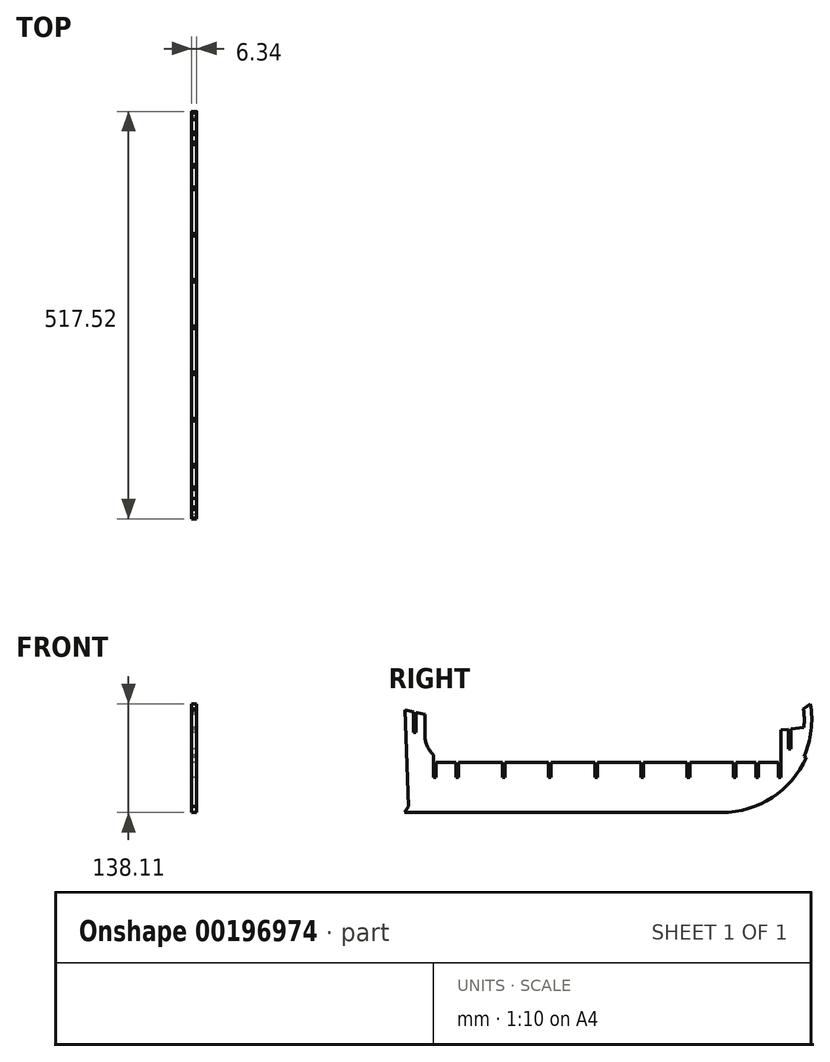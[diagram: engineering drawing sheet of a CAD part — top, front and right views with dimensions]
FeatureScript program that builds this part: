
annotation { "Feature Type Name" : "Feature", "Feature Type Description" : "" }
export const myFeature = defineFeature(function(context is Context, id is Id, definition is map)
    precondition{}
    {
        {
            var Q0;
            Q0=qCreatedBy(makeId("Right.planeOp"),FACE);
            var sketch = newSketch(context, id + "F0", { "sketchPlane" : qUnion([Q0])});
            skLineSegment(sketch, "E0", {"start": v(-201.61, 0) * mm, "end": v(0, 0) * mm});
            skLineSegment(sketch, "E1", {"start": v(0, 0) * mm, "end": v(201.61, 0) * mm});
            skArc(sketch, "E2", {"start": v(201.61, 0) * mm, "mid": v(265.67, 19) * mm, "end": v(309, 69.85) * mm});
            skLineSegment(sketch, "E3", {"start": v(309, 69.85) * mm, "end": v(306.1, 71.14) * mm});
            skLineSegment(sketch, "E4", {"start": v(295.1, 46.34) * mm, "end": v(306.1, 71.14) * mm, "construction": true});
            skArc(sketch, "E5", {"start": v(306.1, 71.14) * mm, "mid": v(315.12, 104.03) * mm, "end": v(314.03, 138.11) * mm});
            skLineSegment(sketch, "E6", {"start": v(315.91, 0) * mm, "end": v(201.61, 0) * mm, "construction": true});
            skLineSegment(sketch, "E7", {"start": v(314.03, 138.11) * mm, "end": v(305.4, 131.76) * mm});
            skArc(sketch, "E8", {"start": v(305.95, 107.95) * mm, "mid": v(306.36, 119.87) * mm, "end": v(305.4, 131.76) * mm});
            skLineSegment(sketch, "E9", {"start": v(305.95, 107.95) * mm, "end": v(289.45, 106.16) * mm});
            skLineSegment(sketch, "E10", {"start": v(289.45, 106.16) * mm, "end": v(289.45, 80.76) * mm});
            skLineSegment(sketch, "E11", {"start": v(289.45, 80.76) * mm, "end": v(286.27, 80.76) * mm});
            skLineSegment(sketch, "E12", {"start": v(286.27, 80.76) * mm, "end": v(286.27, 105.81) * mm});
            skLineSegment(sketch, "E13", {"start": v(286.27, 105.81) * mm, "end": v(276.75, 104.78) * mm});
            skLineSegment(sketch, "E14", {"start": v(276.75, 104.77) * mm, "end": v(276.75, 44.45) * mm});
            skLineSegment(sketch, "E15", {"start": v(276.75, 44.45) * mm, "end": v(273.57, 44.45) * mm});
            skLineSegment(sketch, "E16", {"start": v(273.57, 44.45) * mm, "end": v(273.57, 63.5) * mm});
            skLineSegment(sketch, "E17", {"start": v(273.57, 63.5) * mm, "end": v(248.17, 63.5) * mm});
            skLineSegment(sketch, "E18", {"start": v(248.17, 63.5) * mm, "end": v(248.17, 44.45) * mm});
            skLineSegment(sketch, "E19", {"start": v(248.17, 44.45) * mm, "end": v(245, 44.45) * mm});
            skLineSegment(sketch, "E20", {"start": v(245, 44.45) * mm, "end": v(245, 63.5) * mm});
            skLineSegment(sketch, "E21", {"start": v(245, 63.5) * mm, "end": v(219.6, 63.5) * mm});
            skLineSegment(sketch, "E22", {"start": v(219.6, 63.5) * mm, "end": v(219.6, 44.45) * mm});
            skLineSegment(sketch, "E23", {"start": v(219.6, 44.45) * mm, "end": v(216.42, 44.45) * mm});
            skLineSegment(sketch, "E24", {"start": v(216.42, 44.45) * mm, "end": v(216.42, 63.5) * mm});
            skLineSegment(sketch, "E25", {"start": v(216.42, 63.5) * mm, "end": v(160.86, 63.5) * mm});
            skLineSegment(sketch, "E26", {"start": v(160.86, 63.5) * mm, "end": v(160.86, 44.45) * mm});
            skLineSegment(sketch, "E27", {"start": v(160.86, 44.45) * mm, "end": v(157.68, 44.45) * mm});
            skLineSegment(sketch, "E28", {"start": v(157.68, 44.45) * mm, "end": v(157.68, 63.5) * mm});
            skLineSegment(sketch, "E29", {"start": v(157.68, 63.5) * mm, "end": v(102.12, 63.5) * mm});
            skLineSegment(sketch, "E30", {"start": v(102.12, 63.5) * mm, "end": v(102.12, 44.45) * mm});
            skLineSegment(sketch, "E31", {"start": v(102.12, 44.45) * mm, "end": v(98.95, 44.45) * mm});
            skLineSegment(sketch, "E32", {"start": v(98.95, 44.45) * mm, "end": v(98.95, 63.5) * mm});
            skLineSegment(sketch, "E33", {"start": v(98.95, 63.5) * mm, "end": v(43.38, 63.5) * mm});
            skLineSegment(sketch, "E34", {"start": v(315.91, 117.48) * mm, "end": v(315.91, 0) * mm, "construction": true});
            skArc(sketch, "E35", {"start": v(305.95, 107.95) * mm, "mid": v(272.25, 40.1) * mm, "end": v(201.61, 12.7) * mm, "construction": true});
            skLineSegment(sketch, "E36", {"start": v(43.38, 63.5) * mm, "end": v(43.38, 44.45) * mm});
            skLineSegment(sketch, "E37", {"start": v(43.38, 44.45) * mm, "end": v(40.2, 44.45) * mm});
            skLineSegment(sketch, "E38", {"start": v(40.2, 44.45) * mm, "end": v(40.2, 63.5) * mm});
            skLineSegment(sketch, "E39", {"start": v(40.2, 63.5) * mm, "end": v(-15.35, 63.5) * mm});
            skLineSegment(sketch, "E40", {"start": v(-15.35, 63.5) * mm, "end": v(-15.35, 44.45) * mm});
            skLineSegment(sketch, "E41", {"start": v(-15.35, 44.45) * mm, "end": v(-18.53, 44.45) * mm});
            skLineSegment(sketch, "E42", {"start": v(-18.53, 44.45) * mm, "end": v(-18.53, 63.5) * mm});
            skLineSegment(sketch, "E43", {"start": v(-18.53, 63.5) * mm, "end": v(-74.1, 63.5) * mm});
            skLineSegment(sketch, "E44", {"start": v(-74.1, 63.5) * mm, "end": v(-74.1, 44.45) * mm});
            skLineSegment(sketch, "E45", {"start": v(-74.1, 44.45) * mm, "end": v(-77.27, 44.45) * mm});
            skLineSegment(sketch, "E46", {"start": v(-77.27, 44.45) * mm, "end": v(-77.27, 63.5) * mm});
            skLineSegment(sketch, "E47", {"start": v(-77.27, 63.5) * mm, "end": v(-132.83, 63.5) * mm});
            skLineSegment(sketch, "E48", {"start": v(-132.83, 63.5) * mm, "end": v(-132.83, 44.45) * mm});
            skLineSegment(sketch, "E49", {"start": v(-132.83, 44.45) * mm, "end": v(-136, 44.45) * mm});
            skLineSegment(sketch, "E50", {"start": v(-136, 44.45) * mm, "end": v(-136, 63.5) * mm});
            skLineSegment(sketch, "E51", {"start": v(-136, 63.5) * mm, "end": v(-161.4, 63.5) * mm});
            skLineSegment(sketch, "E52", {"start": v(-161.4, 63.5) * mm, "end": v(-161.4, 44.45) * mm});
            skLineSegment(sketch, "E53", {"start": v(-161.4, 44.45) * mm, "end": v(-164.58, 44.45) * mm});
            skLineSegment(sketch, "E54", {"start": v(-164.58, 44.45) * mm, "end": v(-164.58, 73.03) * mm});
            skArc(sketch, "E55", {"start": v(-175.7, 99.15) * mm, "mid": v(-172.8, 84.95) * mm, "end": v(-164.58, 73.03) * mm});
            skLineSegment(sketch, "E56", {"start": v(-175.7, 99.15) * mm, "end": v(-175.7, 124.55) * mm});
            skLineSegment(sketch, "E57", {"start": v(-175.7, 124.55) * mm, "end": v(-186.5, 127) * mm});
            skLineSegment(sketch, "E58", {"start": v(-186.5, 127) * mm, "end": v(-186.5, 101.6) * mm});
            skLineSegment(sketch, "E59", {"start": v(-186.5, 101.6) * mm, "end": v(-189.68, 101.6) * mm});
            skLineSegment(sketch, "E60", {"start": v(-189.68, 101.6) * mm, "end": v(-189.68, 127.72) * mm});
            skLineSegment(sketch, "E61", {"start": v(-189.68, 127.72) * mm, "end": v(-200.5, 130.18) * mm});
            skLineSegment(sketch, "E62", {"start": v(-200.5, 130.18) * mm, "end": v(-196.35, 7.94) * mm});
            skLineSegment(sketch, "E63", {"start": v(-196.35, 7.94) * mm, "end": v(-201.61, 0) * mm});
            skSolve(sketch);
        }
        {
            var Q0;
            Q0=makeQuery(id+"F0.imprint","IMPRINT",FACE,{"disambiguationData":[TD([[makeQuery(id+"F0.imprint","IMPRINT",EDGE,{"derivedFrom":sQuery(id+"F0.wireOp",EDGE,"E0")}),1.0]])]});
            extrude(context, id + "F1", {"entities" : qUnion([Q0]), "endBound" : BoundingType.SYMMETRIC, "depth" : 6.35 * mm});
        }
    });
